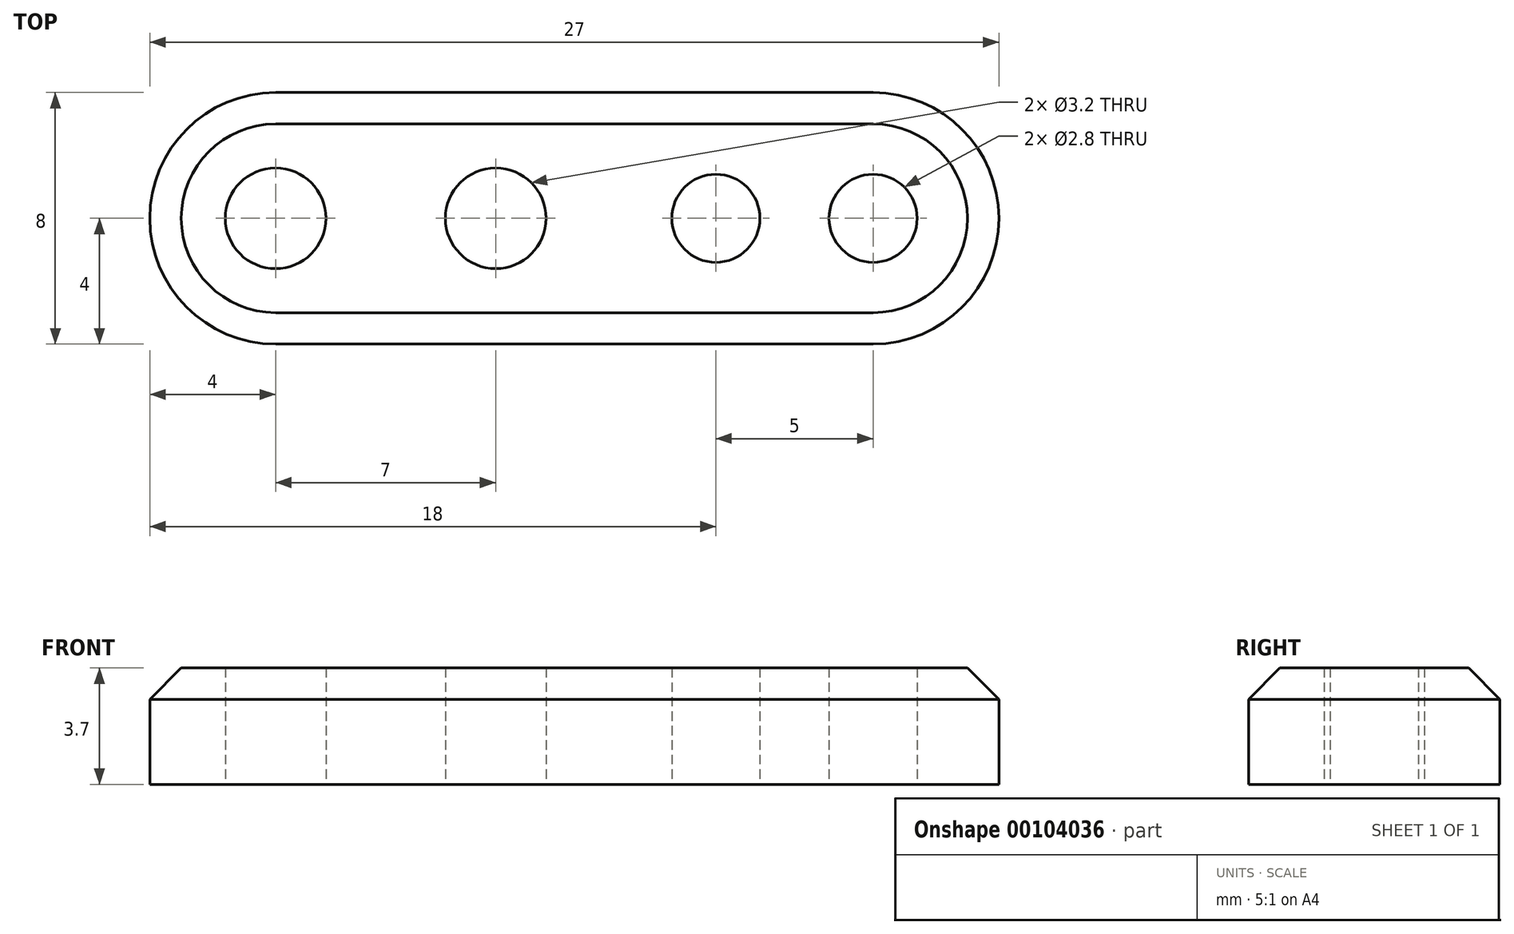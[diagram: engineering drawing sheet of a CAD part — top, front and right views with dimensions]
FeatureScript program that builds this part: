
annotation { "Feature Type Name" : "Feature", "Feature Type Description" : "" }
export const myFeature = defineFeature(function(context is Context, id is Id, definition is map)
    precondition{}
    {
        {
            assignVariable(context, id + "F0", {"name" : "height", "anyValue" : 3.7});
        }
        {
            var Q0;
            Q0=qCreatedBy(makeId("Top.planeOp"),FACE);
            var sketch = newSketch(context, id + "F1", { "sketchPlane" : qUnion([Q0])});
            skLineSegment(sketch, "E0", {"start": v(-9.5, 4) * mm, "end": v(9.5, 4) * mm});
            skLineSegment(sketch, "E1", {"start": v(-9.5, -4) * mm, "end": v(9.5, -4) * mm});
            skArc(sketch, "E2", {"start": v(-9.5, 4) * mm, "mid": v(-13.5, 0) * mm, "end": v(-9.5, -4) * mm});
            skArc(sketch, "E3", {"start": v(9.5, -4) * mm, "mid": v(13.5, 0) * mm, "end": v(9.5, 4) * mm});
            skCircle(sketch, "E4", {"center": v(-9.5, 0) * mm, "radius": 1.6 * mm});
            skCircle(sketch, "E5", {"center": v(-2.5, 0) * mm, "radius": 1.6 * mm});
            skCircle(sketch, "E6", {"center": v(9.5, 0) * mm, "radius": 1.4 * mm});
            skCircle(sketch, "E7", {"center": v(4.5, 0) * mm, "radius": 1.4 * mm});
            skSolve(sketch);
        }
        {
            var Q0;
            Q0=makeQuery(id+"F1.imprint","IMPRINT",FACE,{"disambiguationData":[TD([[makeQuery(id+"F1.imprint","IMPRINT",EDGE,{"derivedFrom":sQuery(id+"F1.wireOp",EDGE,"E0")}),-1.0]])]});
            extrude(context, id + "F2", {"entities" : qUnion([Q0]), "depth" : (getVariable(context, 'height')) * mm});
        }
        {
            var Q0;
            Q0=makeQuery(id+"F2.opExtrude","CAP_EDGE",EDGE,{"disambiguationData":[OSD([sQuery(id+"F1.wireOp",EDGE,"E1")])],"isStart":false});
            var Q1;
            Q1=makeQuery(id+"F2.opExtrude","CAP_EDGE",EDGE,{"disambiguationData":[OSD([sQuery(id+"F1.wireOp",EDGE,"E3")])],"isStart":false});
            var Q2;
            Q2=makeQuery(id+"F2.opExtrude","CAP_EDGE",EDGE,{"disambiguationData":[OSD([sQuery(id+"F1.wireOp",EDGE,"E0")])],"isStart":false});
            var Q3;
            Q3=makeQuery(id+"F2.opExtrude","CAP_EDGE",EDGE,{"disambiguationData":[OSD([sQuery(id+"F1.wireOp",EDGE,"E2")])],"isStart":false});
            chamfer(context, id + "F3", {"entities" : qUnion([Q0, Q1, Q2, Q3]), "width" : 1 * mm, "tangentPropagation" : true});
        }
    });
